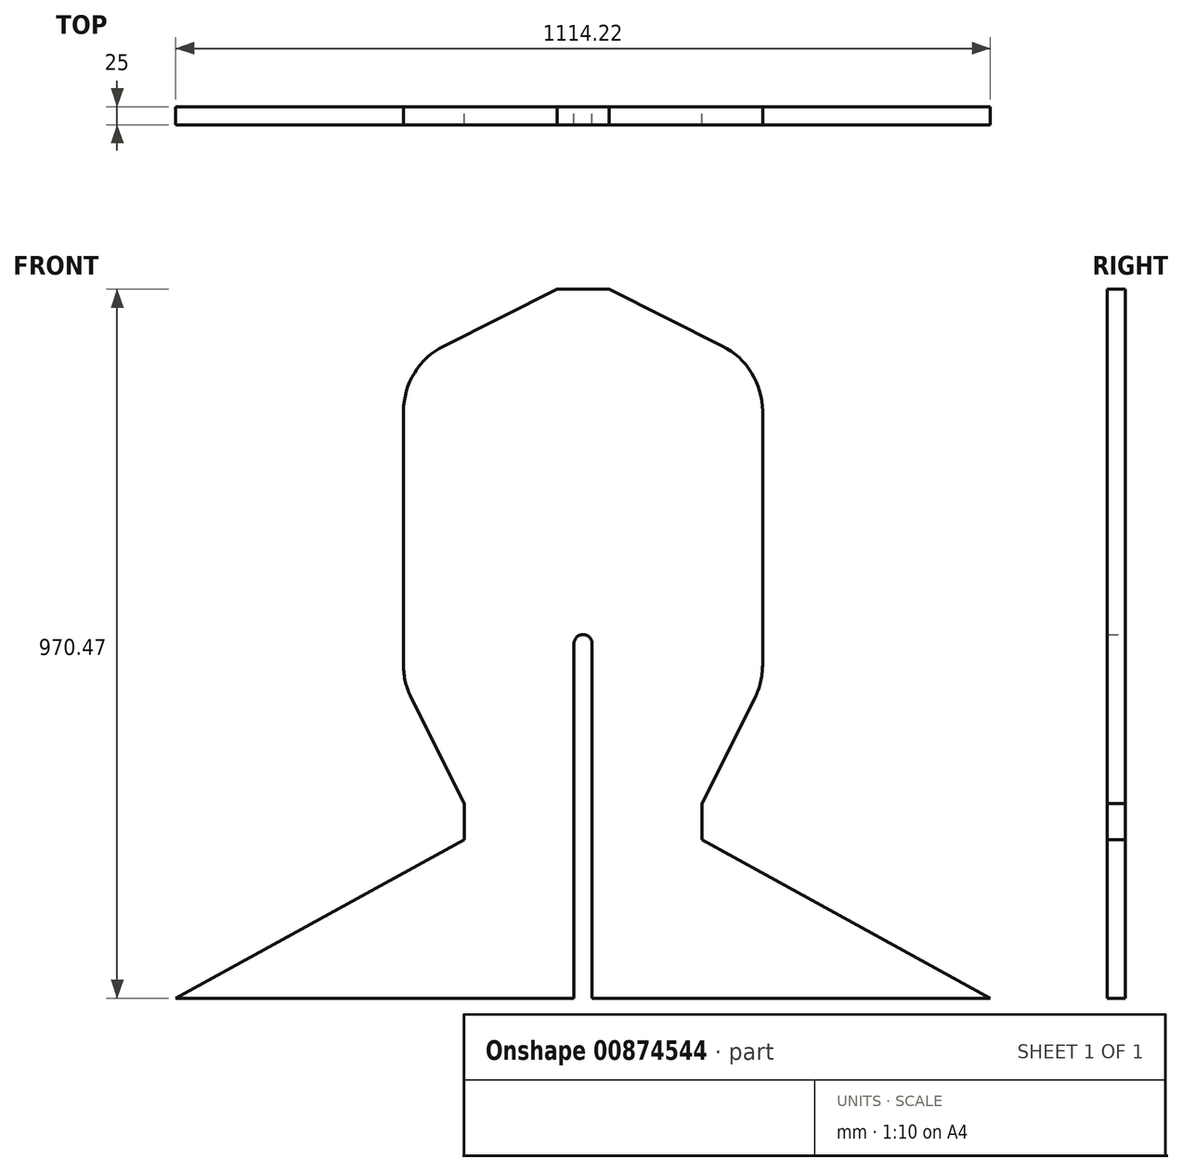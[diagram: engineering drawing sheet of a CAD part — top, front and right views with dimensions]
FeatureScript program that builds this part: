
annotation { "Feature Type Name" : "Feature", "Feature Type Description" : "" }
export const myFeature = defineFeature(function(context is Context, id is Id, definition is map)
    precondition{}
    {
        {
            var Q0;
            Q0=qCreatedBy(makeId("Front.planeOp"),FACE);
            var sketch = newSketch(context, id + "F0", { "sketchPlane" : qUnion([Q0])});
            skLineSegment(sketch, "E0", {"start": v(194.9, 37.13) * mm, "end": v(-199.54, 253.74) * mm});
            skLineSegment(sketch, "E1", {"start": v(-199.54, 253.74) * mm, "end": v(-199.54, 303.74) * mm});
            skLineSegment(sketch, "E2", {"start": v(-199.54, 303.74) * mm, "end": v(-127.25, 447.98) * mm});
            skLineSegment(sketch, "E3", {"start": v(-116.65, 492.79) * mm, "end": v(-116.65, 840.55) * mm});
            skLineSegment(sketch, "E4", {"start": v(-171.83, 929.94) * mm, "end": v(-326.72, 1007.6) * mm});
            skLineSegment(sketch, "E5", {"start": v(-326.72, 1007.6) * mm, "end": v(-397.72, 1007.6) * mm});
            skLineSegment(sketch, "E6", {"start": v(-374.72, 37.13) * mm, "end": v(-374.72, 522.45) * mm});
            skLineSegment(sketch, "E7", {"start": v(-349.72, 37.13) * mm, "end": v(-349.72, 522.45) * mm});
            skPoint(sketch, "E8.visualSharp", {"position": v(-116.65, 902.27) * mm});
            skArc(sketch, "E8.filletArc", {"start": v(-116.65, 840.55) * mm, "mid": v(-131.55, 893.07) * mm, "end": v(-171.83, 929.94) * mm});
            skPoint(sketch, "E9.visualSharp", {"position": v(-116.65, 469.13) * mm});
            skArc(sketch, "E9.filletArc", {"start": v(-127.25, 447.98) * mm, "mid": v(-119.33, 469.76) * mm, "end": v(-116.65, 492.79) * mm});
            skLineSegment(sketch, "E10", {"start": v(-362.22, 1007.6) * mm, "end": v(-362.22, 37.13) * mm, "construction": true});
            skLineSegment(sketch, "E11.MirrorCS", {"start": v(-552.61, 929.94) * mm, "end": v(-397.72, 1007.6) * mm});
            skArc(sketch, "E12.MirrorCS", {"start": v(-607.79, 840.55) * mm, "mid": v(-592.88, 893.07) * mm, "end": v(-552.61, 929.94) * mm});
            skLineSegment(sketch, "E13.MirrorCS", {"start": v(-607.79, 492.79) * mm, "end": v(-607.79, 840.55) * mm});
            skLineSegment(sketch, "E14.MirrorCS", {"start": v(-524.9, 303.74) * mm, "end": v(-597.19, 447.98) * mm});
            skArc(sketch, "E15.MirrorCS", {"start": v(-597.19, 447.98) * mm, "mid": v(-605.1, 469.76) * mm, "end": v(-607.79, 492.79) * mm});
            skLineSegment(sketch, "E16.MirrorCS", {"start": v(-524.9, 253.74) * mm, "end": v(-524.9, 303.74) * mm});
            skLineSegment(sketch, "E17.MirrorCS", {"start": v(-919.33, 37.13) * mm, "end": v(-524.9, 253.74) * mm});
            skLineSegment(sketch, "E18", {"start": v(-919.33, 37.13) * mm, "end": v(-374.72, 37.13) * mm});
            skLineSegment(sketch, "E19.trimOffspring", {"start": v(-349.72, 37.13) * mm, "end": v(194.9, 37.13) * mm});
            skArc(sketch, "E20", {"start": v(-349.72, 522.28) * mm, "mid": v(-362.22, 534.87) * mm, "end": v(-374.72, 522.28) * mm});
            skSolve(sketch);
        }
        {
            var Q0;
            Q0 = qSketchRegion(id + "F0", true);
            extrude(context, id + "F1", {"entities" : qUnion([Q0]), "depth" : 25 * mm, "offsetDistance" : 25 * mm});
        }
    });
